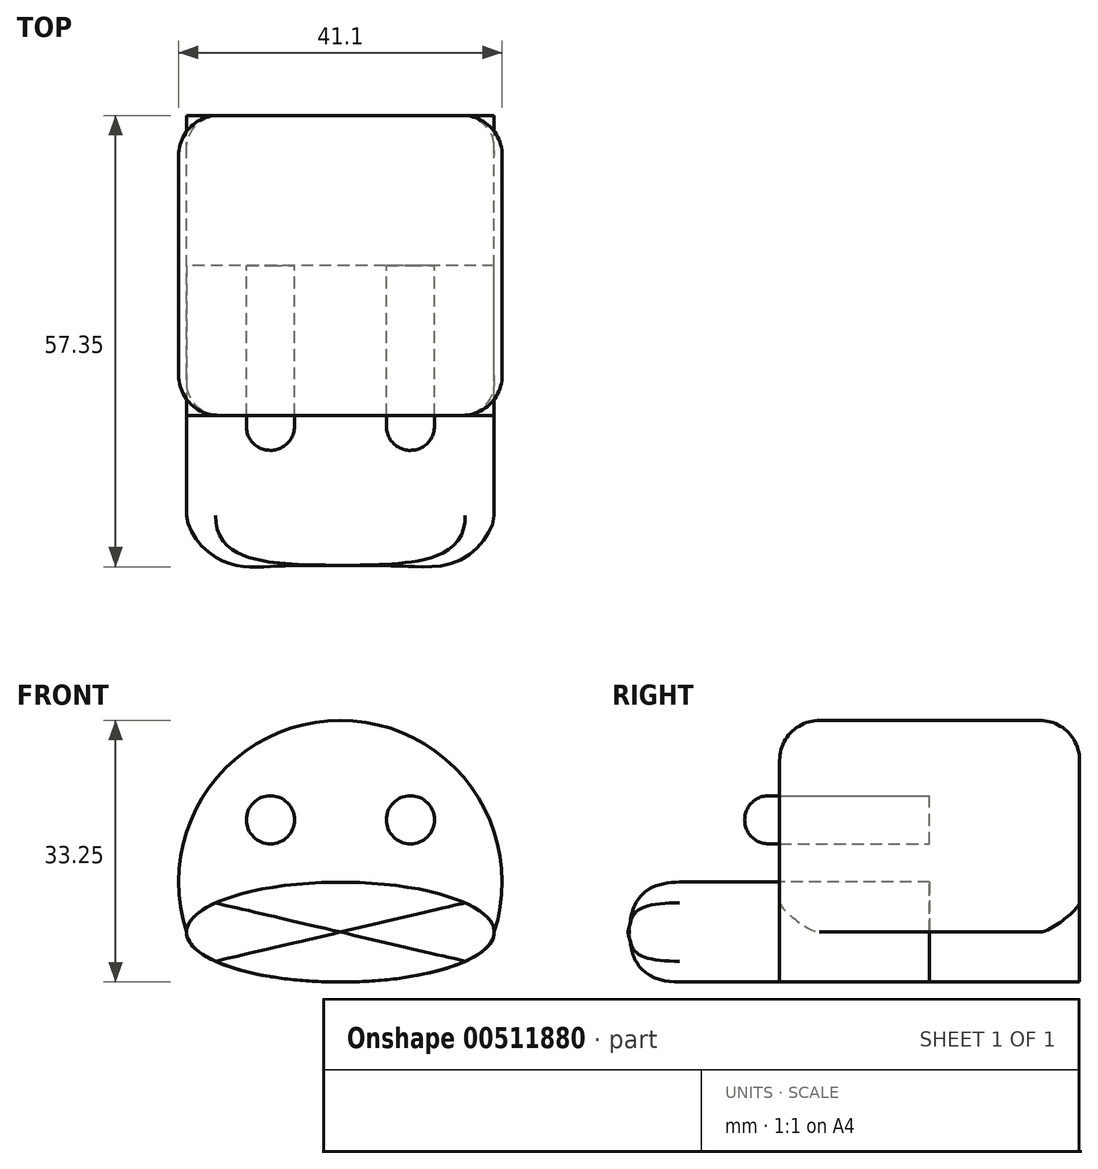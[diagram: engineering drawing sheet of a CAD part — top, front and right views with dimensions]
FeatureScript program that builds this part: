
annotation { "Feature Type Name" : "Feature", "Feature Type Description" : "" }
export const myFeature = defineFeature(function(context is Context, id is Id, definition is map)
    precondition{}
    {
        {
            var Q0;
            Q0=qCreatedBy(makeId("Front.planeOp"),FACE);
            var sketch = newSketch(context, id + "F0", { "sketchPlane" : qUnion([Q0])});
            skArc(sketch, "E0", {"start": v(19.54, 6.35) * mm, "mid": v(0, 33.25) * mm, "end": v(-19.54, 6.35) * mm});
            skArc(sketch, "E1", {"start": v(-19.54, 6.35) * mm, "mid": v(0, 0) * mm, "end": v(19.54, 6.35) * mm, "construction": true});
            skCircle(sketch, "E2", {"center": v(-8.9, 20.62) * mm, "radius": 3.06 * mm});
            skCircle(sketch, "E3", {"center": v(8.9, 20.62) * mm, "radius": 3.06 * mm});
            skEllipse(sketch, "E4", {"center": v(0, 6.35) * mm, "majorRadius": 19.54 * mm, "minorRadius": 6.35 * mm, "majorAxis": v(1, 0)});
            skLineSegment(sketch, "E5.0", {"start": v(0, 6.35) * mm, "end": v(-8.9, 20.62) * mm, "construction": true});
            skLineSegment(sketch, "E5.1", {"start": v(-8.9, 20.62) * mm, "end": v(8.9, 20.62) * mm, "construction": true});
            skLineSegment(sketch, "E5.2", {"start": v(8.9, 20.62) * mm, "end": v(0, 6.35) * mm, "construction": true});
            skLineSegment(sketch, "E6", {"start": v(0, 33.25) * mm, "end": v(0, 20.62) * mm, "construction": true});
            skSolve(sketch);
        }
        {
            var Q0;
            {var subQ0=sQuery(id+"F0.wireOp",EDGE,"E4");var subQ1=sQuery(id+"F0.wireOp",EDGE,"E0");var subQ2=makeQuery(id+"F0.imprint","INTERSECT",VERTEX,{"disambiguationData":[OD(0.0)],"derivedFrom":[subQ1,subQ0]});Q0=makeQuery(id+"F0.imprint","IMPRINT",FACE,{"disambiguationData":[TD([[makeQuery(id+"F0.imprint","IMPRINT",EDGE,{"disambiguationData":[TD([[subQ2,-1.0]])],"derivedFrom":subQ0}),1.0]])]});}
            extrude(context, id + "F1", {"entities" : qUnion([Q0]), "depth" : 38.1 * mm});
        }
        {
            var Q0;
            Q0=makeQuery(id+"F0.imprint","IMPRINT",FACE,{"disambiguationData":[TD([[makeQuery(id+"F0.imprint","IMPRINT",EDGE,{"derivedFrom":sQuery(id+"F0.wireOp",EDGE,"E2")}),1.0]])]});
            var Q1;
            Q1=makeQuery(id+"F0.imprint","IMPRINT",FACE,{"disambiguationData":[TD([[makeQuery(id+"F0.imprint","IMPRINT",EDGE,{"derivedFrom":sQuery(id+"F0.wireOp",EDGE,"E3")}),1.0]])]});
            extrude(context, id + "F2", {"entities" : qUnion([Q0, Q1]), "depth" : 23.5 * mm});
        }
        {
            var Q0;
            {var subQ1=sQuery(id+"F0.wireOp",EDGE,"E0");Q0=makeQuery(id+"F0.imprint","IMPRINT",FACE,{"disambiguationData":[TD([[makeQuery(id+"F0.imprint","IMPRINT",EDGE,{"derivedFrom":subQ1}),1.0]])]});}
            var Q1;
            {var subQ0=sQuery(id+"F0.wireOp",EDGE,"E4");var subQ1=sQuery(id+"F0.wireOp",EDGE,"E1");var subQ2=makeQuery(id+"F0.imprint","INTERSECT",VERTEX,{"disambiguationData":[OD(0.0)],"derivedFrom":[subQ1,subQ0]});Q1=makeQuery(id+"F0.imprint","IMPRINT",FACE,{"disambiguationData":[TD([[makeQuery(id+"F0.imprint","IMPRINT",EDGE,{"disambiguationData":[TD([[subQ2,-1.0]])],"derivedFrom":subQ1}),1.0]])]});}
            var Q2;
            {var subQ0=sQuery(id+"F0.wireOp",EDGE,"E4");var subQ1=sQuery(id+"F0.wireOp",EDGE,"E1");var subQ2=makeQuery(id+"F0.imprint","INTERSECT",VERTEX,{"disambiguationData":[OD(0.0)],"derivedFrom":[subQ1,subQ0]});Q2=makeQuery(id+"F0.imprint","IMPRINT",FACE,{"disambiguationData":[TD([[makeQuery(id+"F0.imprint","IMPRINT",EDGE,{"disambiguationData":[TD([[subQ2,-1.0]])],"derivedFrom":subQ1}),-1.0]])]});}
            var Q3;
            {var subQ0=sQuery(id+"F0.wireOp",EDGE,"E4");var subQ1=sQuery(id+"F0.wireOp",EDGE,"E1");var subQ3=makeQuery(id+"F0.imprint","INTERSECT",VERTEX,{"disambiguationData":[OD(2.0)],"derivedFrom":[subQ1,subQ0]});Q3=makeQuery(id+"F0.imprint","IMPRINT",FACE,{"disambiguationData":[TD([[makeQuery(id+"F0.imprint","IMPRINT",EDGE,{"disambiguationData":[TD([[subQ3,-1.0]])],"derivedFrom":subQ1}),-1.0]])]});}
            var Q4;
            Q4=makeQuery(id+"F0.imprint","IMPRINT",FACE,{"disambiguationData":[TD([[makeQuery(id+"F0.imprint","IMPRINT",EDGE,{"derivedFrom":sQuery(id+"F0.wireOp",EDGE,"E3")}),1.0]])]});
            var Q5;
            Q5=makeQuery(id+"F0.imprint","IMPRINT",FACE,{"disambiguationData":[TD([[makeQuery(id+"F0.imprint","IMPRINT",EDGE,{"derivedFrom":sQuery(id+"F0.wireOp",EDGE,"E2")}),1.0]])]});
            var Q6;
            {var subQ0=sQuery(id+"F0.wireOp",EDGE,"E4");var subQ1=sQuery(id+"F0.wireOp",EDGE,"E0");var subQ2=makeQuery(id+"F0.imprint","INTERSECT",VERTEX,{"disambiguationData":[OD(0.0)],"derivedFrom":[subQ1,subQ0]});Q6=makeQuery(id+"F0.imprint","IMPRINT",FACE,{"disambiguationData":[TD([[makeQuery(id+"F0.imprint","IMPRINT",EDGE,{"disambiguationData":[TD([[subQ2,-1.0]])],"derivedFrom":subQ0}),1.0]])]});}
            extrude(context, id + "F3", {"entities" : qUnion([Q0, Q1, Q2, Q3, Q4, Q5, Q6]), "endBound" : BoundingType.SYMMETRIC, "depth" : 38.1 * mm});
        }
        {
            var Q0;
            Q0=makeQuery(id+"F3.opExtrude","CAP_EDGE",EDGE,{"disambiguationData":[OSD([sQuery(id+"F0.wireOp",EDGE,"E0")])],"isStart":false});
            var Q1;
            Q1=makeQuery(id+"F3.opExtrude","CAP_EDGE",EDGE,{"disambiguationData":[OSD([sQuery(id+"F0.wireOp",EDGE,"E0")])],"isStart":true});
            fillet(context, id + "F4", {"entities" : qUnion([Q0, Q1]), "radius" : 5.08 * mm, "tangentPropagation" : true, "allowEdgeOverflow" : false});
        }
        {
            var Q0;
            Q0=makeQuery(id+"F1.opExtrude","CAP_EDGE",EDGE,{"disambiguationData":[OSD([sQuery(id+"F0.wireOp",EDGE,"E4")])],"isStart":false});
            fillet(context, id + "F5", {"entities" : qUnion([Q0]), "radius" : 6.35 * mm, "tangentPropagation" : true, "rho" : .5, "crossSection" : FilletCrossSection.CONIC, "allowEdgeOverflow" : false});
        }
        {
            var Q0;
            Q0=makeQuery(id+"F2.opExtrude","CAP_EDGE",EDGE,{"disambiguationData":[OSD([sQuery(id+"F0.wireOp",EDGE,"E2")])],"isStart":false});
            var Q1;
            Q1=makeQuery(id+"F2.opExtrude","CAP_EDGE",EDGE,{"disambiguationData":[OSD([sQuery(id+"F0.wireOp",EDGE,"E3")])],"isStart":false});
            fillet(context, id + "F6", {"entities" : qUnion([Q0, Q1]), "radius" : 3.05 * mm, "tangentPropagation" : true, "allowEdgeOverflow" : false});
        }
    });
